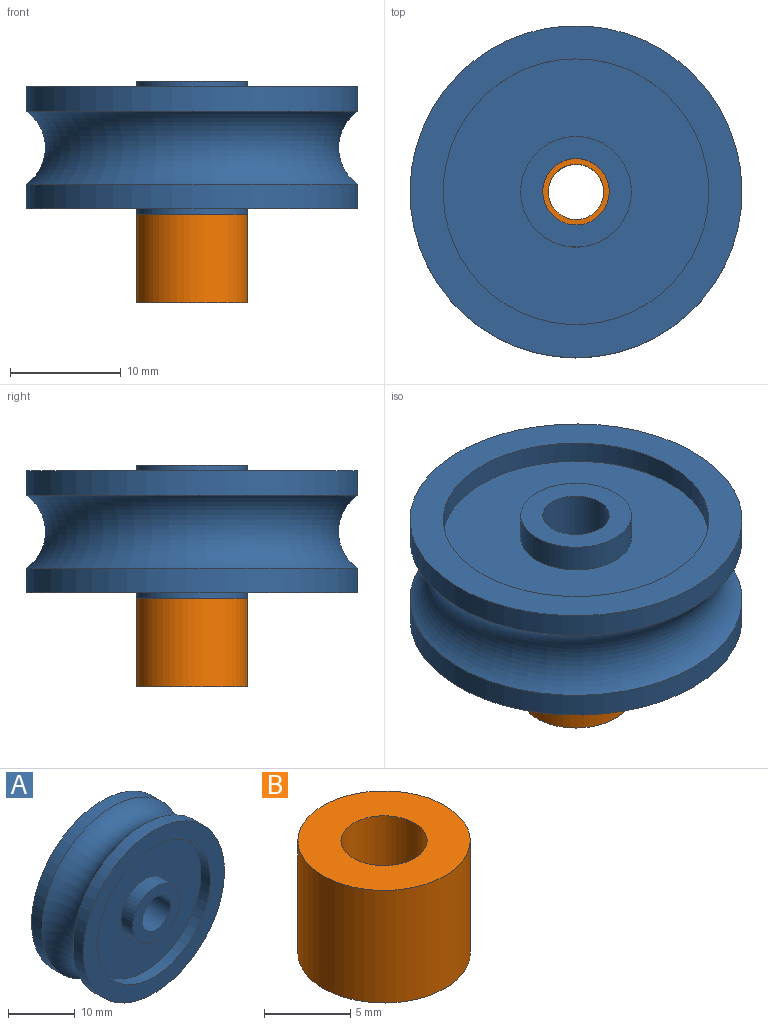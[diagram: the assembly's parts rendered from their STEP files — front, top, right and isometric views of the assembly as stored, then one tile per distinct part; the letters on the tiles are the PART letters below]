
ASSEMBLY  parts=2 mates=1
PART A: 14 faces, bbox 37.3x12x37.3 mm
  f0: torus R=17.25mm, axis (0,1,0), area 677.8mm2, adj f1,f8
  f1: cylinder r=15mm len=30mm, axis (0,1,0), area 206.7mm2, adj f0,f2
  f2: plane 30x30mm, normal (0,-1,0), area 254.5mm2, adj f1,f3
  f3: cylinder r=12mm len=24mm, axis (0,-1,0), area 150.8mm2, adj f2,f4
  f4: plane 24x24mm, normal (0,-1,0), area 373.8mm2, adj f3,f7
  f5: cylinder r=3mm len=12mm, axis (0,1,0), area 226.2mm2, adj f6,f12
  f6: plane 10x10mm, normal (0,-1,0), area 50.3mm2, adj f5,f7
  f7: cylinder r=5mm len=10mm, axis (0,1,0), area 78.5mm2, adj f4,f6
  f8: cylinder r=15mm len=30mm, axis (0,-1,0), area 206.7mm2, adj f0,f9
  f9: plane 30x30mm, normal (0,1,0), area 254.5mm2, adj f8,f10
  f10: cylinder r=12mm len=24mm, axis (0,1,0), area 150.8mm2, adj f9,f11
  f11: plane 24x24mm, normal (0,1,0), area 373.8mm2, adj f10,f13
  f12: plane 10x10mm, normal (0,1,0), area 50.3mm2, adj f5,f13
  f13: cylinder r=5mm len=10mm, axis (0,-1,0), area 78.5mm2, adj f11,f12
PART B: 4 faces, bbox 10x10x8 mm
  f0: cylinder r=2.5mm len=8mm, axis (0,0,-1), area 125.7mm2, adj f2,f3
  f1: cylinder r=5mm len=10mm, axis (0,0,-1), area 251.3mm2, adj f2,f3
  f2: plane 10x10mm, normal (0,0,1), area 58.9mm2, adj f0,f1
  f3: plane 10x10mm, normal (0,0,-1), area 58.9mm2, adj f0,f1
PLACE A rot(axis=(1,0,0),90deg) t=(0.06,0.08,18.67)mm
PLACE B rot(axis=(1,0,0),180deg) t=(0.06,0.08,12.67)mm
MATE revolute A.f7 <-> B.f0  axis (0,0,-1) through (0.06,0.08,12.67)mm
